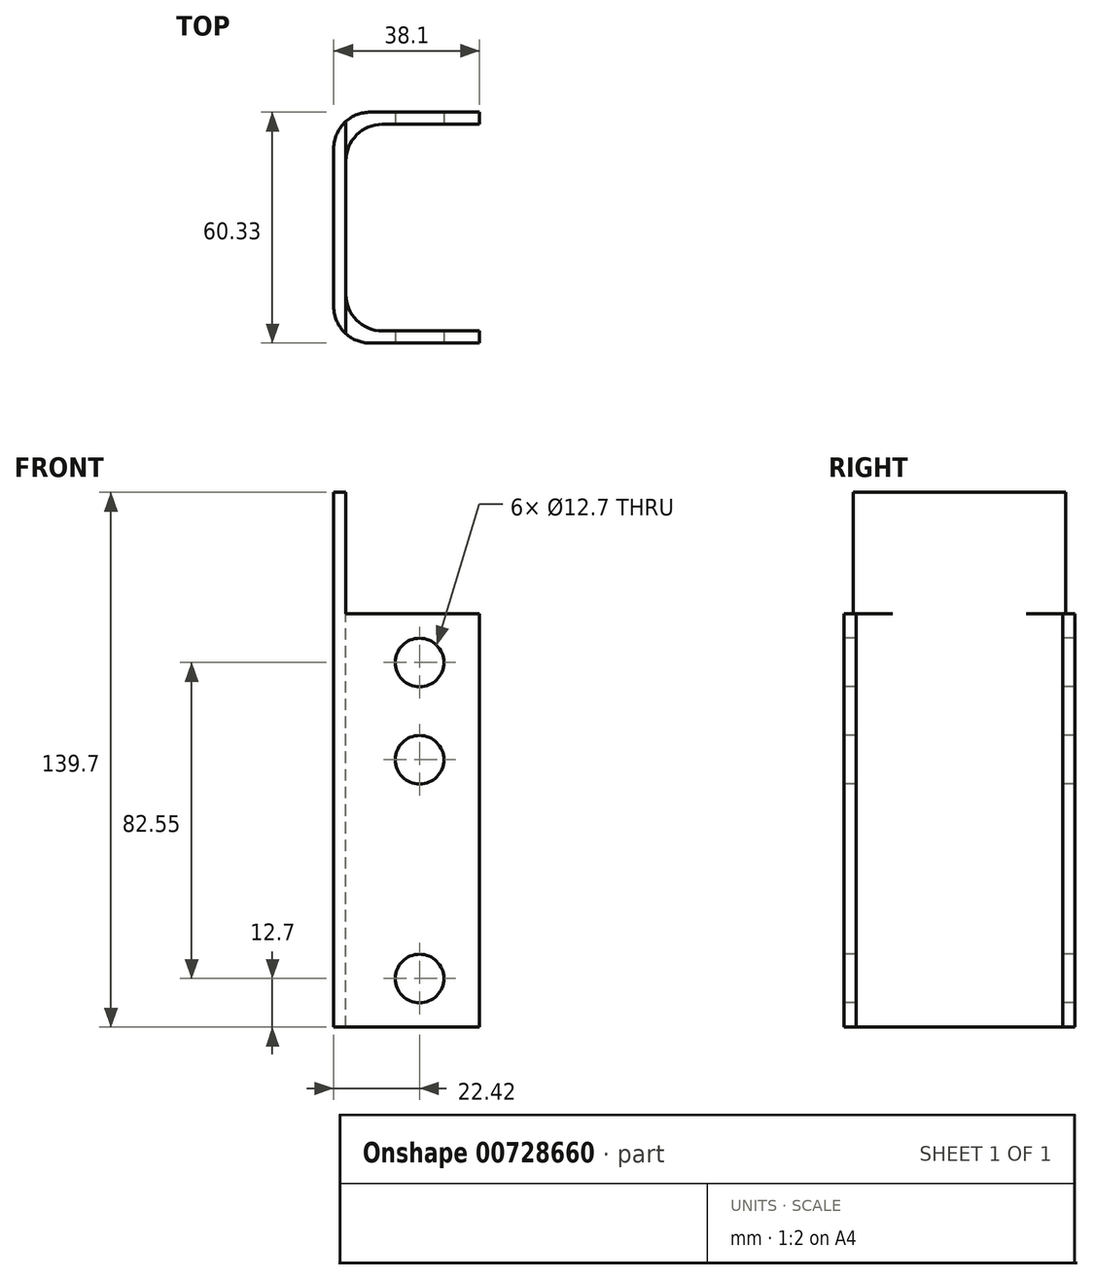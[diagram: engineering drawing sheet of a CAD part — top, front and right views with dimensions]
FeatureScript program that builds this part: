
annotation { "Feature Type Name" : "Feature", "Feature Type Description" : "" }
export const myFeature = defineFeature(function(context is Context, id is Id, definition is map)
    precondition{}
    {
        {
            var Q0;
            Q0=qCreatedBy(makeId("Top.planeOp"),FACE);
            var sketch = newSketch(context, id + "F0", { "sketchPlane" : qUnion([Q0])});
            skLineSegment(sketch, "E0.bottom", {"start": v(0, 0) * mm, "end": v(38.1, 0) * mm});
            skLineSegment(sketch, "E0.top", {"start": v(0, 60.33) * mm, "end": v(38.1, 60.33) * mm});
            skLineSegment(sketch, "E0.left", {"start": v(0, 0) * mm, "end": v(0, 60.33) * mm});
            skLineSegment(sketch, "E0.right", {"start": v(38.1, 0) * mm, "end": v(38.1, 60.33) * mm});
            skSolve(sketch);
        }
        {
            var Q0;
            Q0=makeQuery(id+"F0.imprint","IMPRINT",FACE,{"disambiguationData":[TD([[makeQuery(id+"F0.imprint","IMPRINT",EDGE,{"derivedFrom":sQuery(id+"F0.wireOp",EDGE,"E0.bottom")}),1.0]])]});
            extrude(context, id + "F1", {"entities" : qUnion([Q0]), "depth" : 139.7 * mm, "offsetDistance" : 25.4 * mm});
        }
        {
            var Q0;
            Q0=makeQuery(id+"F1.opExtrude","CAP_FACE",FACE,{"disambiguationData":[OSD([sQuery(id+"F0.wireOp",EDGE,"E0.bottom"),sQuery(id+"F0.wireOp",EDGE,"E0.top"),sQuery(id+"F0.wireOp",EDGE,"E0.left"),sQuery(id+"F0.wireOp",EDGE,"E0.right")])],"isStart":false});
            var sketch = newSketch(context, id + "F2", { "sketchPlane" : qUnion([Q0])});
            skLineSegment(sketch, "E1.bottom", {"start": v(38.1, 57.15) * mm, "end": v(3.17, 57.15) * mm});
            skLineSegment(sketch, "E1.top", {"start": v(38.1, 3.17) * mm, "end": v(3.17, 3.17) * mm});
            skLineSegment(sketch, "E1.left", {"start": v(38.1, 57.15) * mm, "end": v(38.1, 3.17) * mm});
            skLineSegment(sketch, "E1.right", {"start": v(3.17, 57.15) * mm, "end": v(3.17, 3.17) * mm});
            skSolve(sketch);
        }
        {
            var Q0;
            Q0=makeQuery(id+"F2.imprint","IMPRINT",FACE,{"disambiguationData":[TD([[makeQuery(id+"F2.imprint","IMPRINT",EDGE,{"derivedFrom":sQuery(id+"F2.wireOp",EDGE,"E1.bottom")}),1.0]])]});
            extrude(context, id + "F3", {"entities" : qUnion([Q0]), "operationType" : NewBodyOperationType.REMOVE, "oppositeDirection" : true, "depth" : 762 * mm, "offsetDistance" : 25.4 * mm});
        }
        {
            var Q0;
            Q0=makeQuery(id+"F1.opExtrude","SWEPT_FACE",FACE,{"disambiguationData":[OSD([sQuery(id+"F0.wireOp",EDGE,"E0.bottom")])]});
            var sketch = newSketch(context, id + "F4", { "sketchPlane" : qUnion([Q0])});
            skLineSegment(sketch, "E2.bottom", {"start": v(3.18, 139.7) * mm, "end": v(38.1, 139.7) * mm});
            skLineSegment(sketch, "E2.top", {"start": v(3.18, 107.95) * mm, "end": v(38.1, 107.95) * mm});
            skLineSegment(sketch, "E2.left", {"start": v(3.18, 139.7) * mm, "end": v(3.18, 107.95) * mm});
            skLineSegment(sketch, "E2.right", {"start": v(38.1, 139.7) * mm, "end": v(38.1, 107.95) * mm});
            skSolve(sketch);
        }
        {
            var Q0;
            Q0=makeQuery(id+"F4.imprint","IMPRINT",FACE,{"disambiguationData":[TD([[makeQuery(id+"F4.imprint","IMPRINT",EDGE,{"derivedFrom":sQuery(id+"F4.wireOp",EDGE,"E2.bottom")}),-1.0]])]});
            extrude(context, id + "F5", {"entities" : qUnion([Q0]), "operationType" : NewBodyOperationType.REMOVE, "oppositeDirection" : true, "depth" : 85.34 * mm, "offsetDistance" : 25.4 * mm});
        }
        {
            var Q0;
            Q0=makeQuery(id+"F3.boolean.opBoolean","COPY",EDGE,{"derivedFrom":makeQuery(id+"F3.opExtrude","SWEPT_EDGE",EDGE,{"disambiguationData":[OSD([sQuery(id+"F2.wireOp",EDGE,"E1.bottom"),sQuery(id+"F2.wireOp",EDGE,"E1.right")])]})});
            var Q1;
            Q1=makeQuery(id+"F3.boolean.opBoolean","COPY",EDGE,{"derivedFrom":makeQuery(id+"F3.opExtrude","SWEPT_EDGE",EDGE,{"disambiguationData":[OSD([sQuery(id+"F2.wireOp",EDGE,"E1.top"),sQuery(id+"F2.wireOp",EDGE,"E1.right")])]})});
            var Q2;
            Q2=makeQuery(id+"F1.opExtrude","SWEPT_EDGE",EDGE,{"disambiguationData":[OSD([sQuery(id+"F0.wireOp",EDGE,"E0.bottom"),sQuery(id+"F0.wireOp",EDGE,"E0.left")])]});
            var Q3;
            Q3=makeQuery(id+"F1.opExtrude","SWEPT_EDGE",EDGE,{"disambiguationData":[OSD([sQuery(id+"F0.wireOp",EDGE,"E0.top"),sQuery(id+"F0.wireOp",EDGE,"E0.left")])]});
            fillet(context, id + "F6", {"entities" : qUnion([Q0, Q1, Q2, Q3]), "radius" : 9.52 * mm, "tangentPropagation" : true, "allowEdgeOverflow" : false});
        }
        {
            var Q0;
            Q0=makeQuery(id+"F1.opExtrude","SWEPT_FACE",FACE,{"disambiguationData":[OSD([sQuery(id+"F0.wireOp",EDGE,"E0.bottom")])]});
            var sketch = newSketch(context, id + "F7", { "sketchPlane" : qUnion([Q0])});
            skLineSegment(sketch, "E3", {"start": v(22.42, 95.25) * mm, "end": v(22.42, 12.7) * mm});
            skSolve(sketch);
        }
        {
            var Q0;
            Q0=sQuery(id+"F7.wireOp",VERTEX,"E3.start");
            var Q1;
            Q1=sQuery(id+"F7.wireOp",VERTEX,"E3.end");
            var Q2;
            Q2=makeQuery(id+"F1.opExtrude","SWEPT_BODY",BODY,{"disambiguationData":[OSD([sQuery(id+"F0.wireOp",EDGE,"E0.bottom"),sQuery(id+"F0.wireOp",EDGE,"E0.top"),sQuery(id+"F0.wireOp",EDGE,"E0.left"),sQuery(id+"F0.wireOp",EDGE,"E0.right")])]});
            hole(context, id + "F8", {"style" : HoleStyle.SIMPLE, "endStyle" : HoleEndStyle.BLIND, "holeDiameter" : 12.7 * mm, "majorDiameter" : 6.35 * mm, "holeDepth" : 127 * mm, "isTappedThrough" : true, "tappedDepth" : 12.7 * mm, "tapClearance" : 3, "locations" : qUnion([Q0, Q1]), "scope" : qUnion([Q2])});
        }
        {
            var Q0;
            Q0=makeQuery(id+"F1.opExtrude","SWEPT_FACE",FACE,{"disambiguationData":[OSD([sQuery(id+"F0.wireOp",EDGE,"E0.bottom")])]});
            var sketch = newSketch(context, id + "F9", { "sketchPlane" : qUnion([Q0])});
            skLineSegment(sketch, "E4", {"start": v(22.42, 95.25) * mm, "end": v(22.42, 69.85) * mm});
            skSolve(sketch);
        }
        {
            var Q0;
            Q0=sQuery(id+"F9.wireOp",VERTEX,"E4.end");
            var Q1;
            Q1=makeQuery(id+"F1.opExtrude","SWEPT_BODY",BODY,{"disambiguationData":[OSD([sQuery(id+"F0.wireOp",EDGE,"E0.bottom"),sQuery(id+"F0.wireOp",EDGE,"E0.top"),sQuery(id+"F0.wireOp",EDGE,"E0.left"),sQuery(id+"F0.wireOp",EDGE,"E0.right")])]});
            hole(context, id + "F10", {"style" : HoleStyle.SIMPLE, "endStyle" : HoleEndStyle.BLIND, "holeDiameter" : 12.7 * mm, "majorDiameter" : 6.35 * mm, "holeDepth" : 127 * mm, "isTappedThrough" : true, "tappedDepth" : 12.7 * mm, "tapClearance" : 3, "locations" : qUnion([Q0]), "scope" : qUnion([Q1])});
        }
    });
